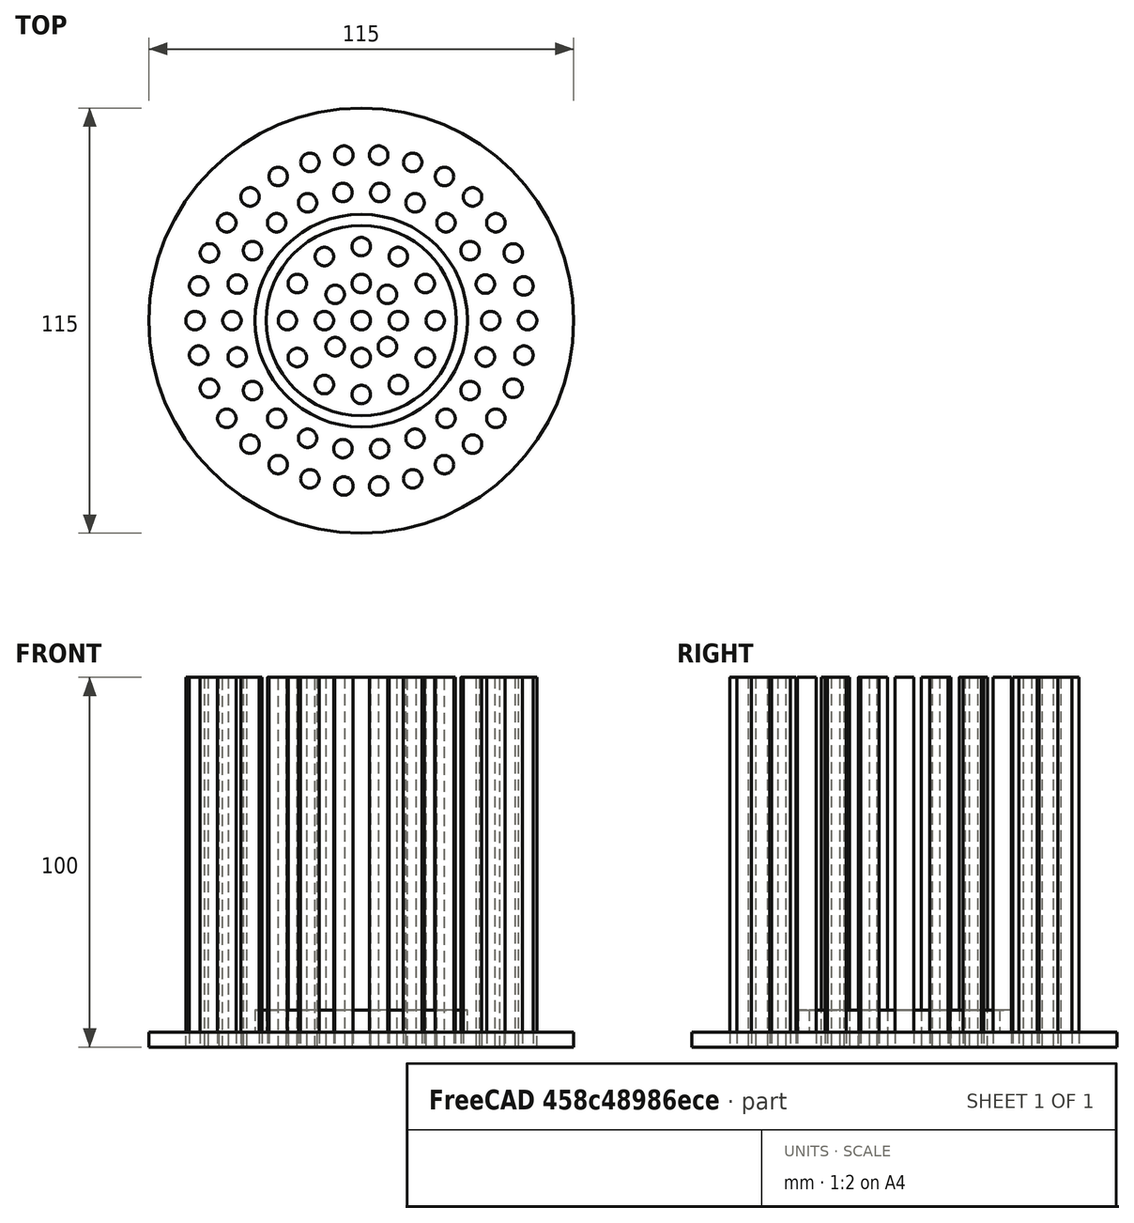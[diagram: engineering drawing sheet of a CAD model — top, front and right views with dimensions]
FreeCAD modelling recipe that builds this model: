
FCSTD DOCUMENT  (FreeCAD 0.15R4671 (Git))
Label: Back Door Drain
License: All rights reserved
LicenseURL: http://en.wikipedia.org/wiki/All_rights_reserved
objects: Part::Extrusion×10, Part::Part2DObjectPython×5, Part::Cut×5, Part::FeaturePython×4, Sketcher::SketchObject×2, PartDesign::Pad×2, Part::MultiFuse×1
note: 31 computed .brp shape members not serialized (recipe doc carries the construction recipe); baked Part::Feature solids carry a one-line shape summary decoded from their .brp

FEATURE [Sketcher::SketchObject] Sketch
  sketch-geometry (1):
    g0: Circle CenterX=0 CenterY=0 CenterZ=0 NormalX=0 NormalY=0 NormalZ=1 Radius=57.5
  constraints (2):
    c: Coincident(g0,g-1)
    c: Radius(g0) = 57.5
FEATURE [PartDesign::Pad] Pad  label="Top"
  Length = 4
  Length2 = 100
  Sketch = -> Sketch
  Type = 0
FEATURE [Sketcher::SketchObject] Sketch001
  sketch-geometry (2):
    g0: Circle CenterX=0 CenterY=0 CenterZ=0 NormalX=0 NormalY=0 NormalZ=1 Radius=28.75
    g1: Circle CenterX=0 CenterY=0 CenterZ=0 NormalX=0 NormalY=0 NormalZ=1 Radius=25.75
  constraints (4):
    c: PointOnObject(g0,g-1)
    c: Radius(g0) = 28.75
    c: Coincident(g1,g-1)
    c: Radius(g1) = 25.75
FEATURE [PartDesign::Pad] Pad001  label="Ring"
  Length = 10
  Length2 = 100
  Sketch = -> Sketch001
  Type = 0
FEATURE [Part::Part2DObjectPython] Circle  # Draft 2D object (typed FeaturePython)
  FirstAngle = 0
  LastAngle = 0
  MakeFace = true
  Radius = 2.5
FEATURE [Part::Part2DObjectPython] Circle001  # Draft 2D object (typed FeaturePython)
  FirstAngle = 0
  LastAngle = 0
  MakeFace = true
  Placement = pos=(10,0,0) rot=(0,0,1;0rad)
  Radius = 2.5
FEATURE [Part::Part2DObjectPython] Circle002  # Draft 2D object (typed FeaturePython)
  FirstAngle = 0
  LastAngle = 0
  MakeFace = true
  Placement = pos=(20,0,0) rot=(0,0,1;0rad)
  Radius = 2.5
FEATURE [Part::Part2DObjectPython] Circle003  # Draft 2D object (typed FeaturePython)
  FirstAngle = 0
  LastAngle = 0
  MakeFace = true
  Placement = pos=(35,0,0) rot=(0,0,1;0rad)
  Radius = 2.5
FEATURE [Part::Part2DObjectPython] Circle004  # Draft 2D object (typed FeaturePython)
  FirstAngle = 0
  LastAngle = 0
  MakeFace = true
  Placement = pos=(45,0,0) rot=(0,0,1;0rad)
  Radius = 2.5
FEATURE [Part::FeaturePython] Array  # Draft array (typed FeaturePython)
  Angle = 360
  ArrayType = 1
  Axis = (0,0,1)
  Base = -> Circle001
  Center = (0,0,0)
  Fuse = false
  IntervalAxis = (0,0,0)
  IntervalX = (1,0,0)
  IntervalY = (0,1,0)
  IntervalZ = (0,0,0)
  NumberPolar = 8
  NumberX = 2
  NumberY = 2
  NumberZ = 1
FEATURE [Part::FeaturePython] Array001  # Draft array (typed FeaturePython)
  Angle = 360
  ArrayType = 1
  Axis = (0,0,1)
  Base = -> Circle002
  Center = (0,0,0)
  Fuse = false
  IntervalAxis = (0,0,0)
  IntervalX = (1,0,0)
  IntervalY = (0,1,0)
  IntervalZ = (0,0,0)
  NumberPolar = 12
  NumberX = 2
  NumberY = 2
  NumberZ = 1
FEATURE [Part::FeaturePython] Array002  # Draft array (typed FeaturePython)
  Angle = 360
  ArrayType = 1
  Axis = (0,0,1)
  Base = -> Circle003
  Center = (0,0,0)
  Fuse = false
  IntervalAxis = (0,0,0)
  IntervalX = (1,0,0)
  IntervalY = (0,1,0)
  IntervalZ = (0,0,0)
  NumberPolar = 22
  NumberX = 2
  NumberY = 2
  NumberZ = 1
FEATURE [Part::FeaturePython] Array003  # Draft array (typed FeaturePython)
  Angle = 360
  ArrayType = 1
  Axis = (0,0,1)
  Base = -> Circle004
  Center = (0,0,0)
  Fuse = false
  IntervalAxis = (0,0,0)
  IntervalX = (1,0,0)
  IntervalY = (0,1,0)
  IntervalZ = (0,0,0)
  NumberPolar = 30
  NumberX = 2
  NumberY = 2
  NumberZ = 1
FEATURE [Part::Extrusion] Extrude
  Base = -> Circle
  Dir = (0,0,100)
  Solid = false
FEATURE [Part::Extrusion] Extrude001
  Base = -> Array
  Dir = (0,0,100)
  Solid = false
FEATURE [Part::Extrusion] Extrude002
  Base = -> Array001
  Dir = (0,0,100)
  Solid = false
FEATURE [Part::Extrusion] Extrude003
  Base = -> Array002
  Dir = (0,0,100)
  Solid = false
FEATURE [Part::Extrusion] Extrude004
  Base = -> Array003
  Dir = (0,0,100)
  Solid = false
FEATURE [Part::Extrusion] Extrude005
  Base = -> Circle
  Dir = (0,0,100)
  Solid = false
FEATURE [Part::Extrusion] Extrude006
  Base = -> Array
  Dir = (0,0,100)
  Solid = false
FEATURE [Part::Extrusion] Extrude007
  Base = -> Array001
  Dir = (0,0,100)
  Solid = false
FEATURE [Part::Extrusion] Extrude008
  Base = -> Array002
  Dir = (0,0,100)
  Solid = false
FEATURE [Part::Extrusion] Extrude009
  Base = -> Array003
  Dir = (0,0,100)
  Solid = false
FEATURE [Part::Cut] Cut
  Base = -> Pad
  Tool = -> Extrude004
FEATURE [Part::Cut] Cut001
  Base = -> Cut
  Tool = -> Extrude003
FEATURE [Part::Cut] Cut002
  Base = -> Cut001
  Tool = -> Extrude002
FEATURE [Part::Cut] Cut003
  Base = -> Cut002
  Tool = -> Extrude001
FEATURE [Part::Cut] Cut004
  Base = -> Cut003
  Tool = -> Extrude
FEATURE [Part::MultiFuse] Fusion
  Shapes = -> [Pad001,Cut004]
